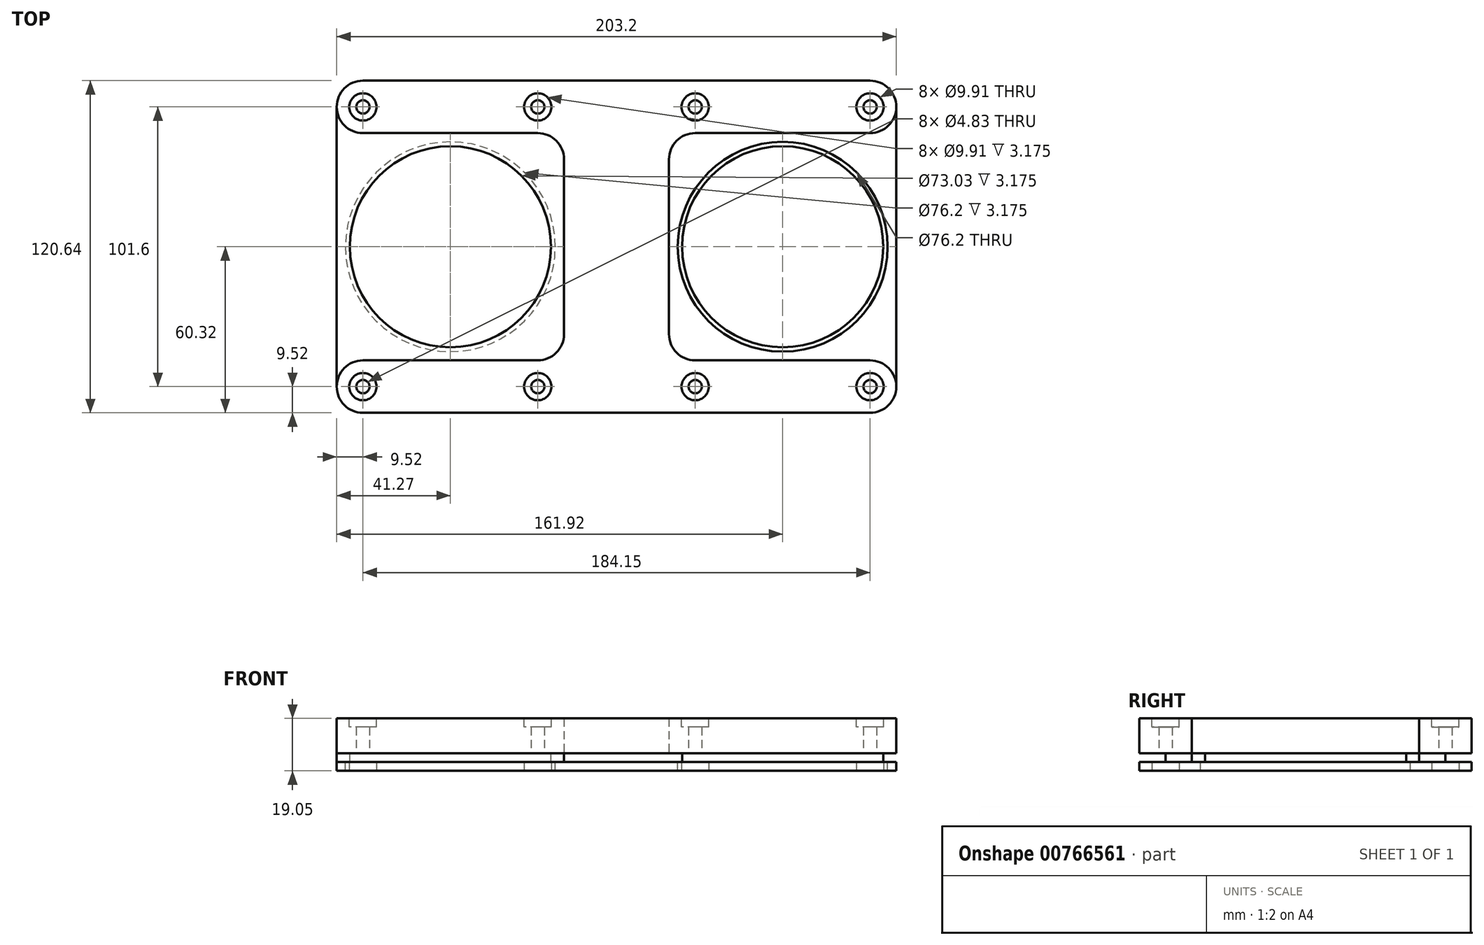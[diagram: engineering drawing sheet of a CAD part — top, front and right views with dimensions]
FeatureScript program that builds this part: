
annotation { "Feature Type Name" : "Feature", "Feature Type Description" : "" }
export const myFeature = defineFeature(function(context is Context, id is Id, definition is map)
    precondition{}
    {
        {
            var Q0;
            Q0=qCreatedBy(makeId("Top.planeOp"),FACE);
            var sketch = newSketch(context, id + "F0", { "sketchPlane" : qUnion([Q0])});
            skLineSegment(sketch, "E0.bottom", {"start": v(-31.75, -41.28) * mm, "end": v(31.75, -41.28) * mm});
            skLineSegment(sketch, "E0.top", {"start": v(-31.75, 41.28) * mm, "end": v(31.75, 41.28) * mm});
            skLineSegment(sketch, "E0.right", {"start": v(41.28, -31.75) * mm, "end": v(41.27, 31.75) * mm});
            skCircle(sketch, "E1", {"center": v(-31.75, -31.75) * mm, "radius": 4.76 * mm});
            skCircle(sketch, "E2", {"center": v(31.75, -31.75) * mm, "radius": 4.76 * mm});
            skCircle(sketch, "E3", {"center": v(31.75, 31.75) * mm, "radius": 4.76 * mm});
            skCircle(sketch, "E4", {"center": v(-31.75, 31.75) * mm, "radius": 4.76 * mm});
            skPoint(sketch, "E5.visualSharp", {"position": v(-41.28, 41.28) * mm});
            skPoint(sketch, "E6.visualSharp", {"position": v(41.28, 41.28) * mm});
            skArc(sketch, "E6.filletArc", {"start": v(41.28, 31.75) * mm, "mid": v(38.49, 38.49) * mm, "end": v(31.75, 41.28) * mm});
            skPoint(sketch, "E7.visualSharp", {"position": v(41.28, -41.28) * mm});
            skArc(sketch, "E7.filletArc", {"start": v(31.75, -41.27) * mm, "mid": v(38.49, -38.49) * mm, "end": v(41.27, -31.75) * mm});
            skPoint(sketch, "E8.visualSharp", {"position": v(-41.27, -41.28) * mm});
            skLineSegment(sketch, "E9.0", {"start": v(-31.75, -60.33) * mm, "end": v(31.75, -60.33) * mm});
            skLineSegment(sketch, "E9.1", {"start": v(-31.75, 60.33) * mm, "end": v(31.75, 60.33) * mm});
            skArc(sketch, "E10", {"start": v(-31.75, 60.33) * mm, "mid": v(-41.28, 50.8) * mm, "end": v(-31.75, 41.28) * mm});
            skCircle(sketch, "E11", {"center": v(-31.75, 50.8) * mm, "radius": 2.41 * mm});
            skCircle(sketch, "E12", {"center": v(31.75, 50.8) * mm, "radius": 2.41 * mm});
            skArc(sketch, "E13", {"start": v(-31.75, -41.28) * mm, "mid": v(-41.27, -50.8) * mm, "end": v(-31.75, -60.33) * mm});
            skCircle(sketch, "E14", {"center": v(-31.75, -50.8) * mm, "radius": 2.41 * mm});
            skCircle(sketch, "E15", {"center": v(31.75, -50.8) * mm, "radius": 2.41 * mm});
            skLineSegment(sketch, "E16.MirrorCS", {"start": v(152.4, -60.32) * mm, "end": v(88.9, -60.32) * mm});
            skLineSegment(sketch, "E17.MirrorCS", {"start": v(152.4, -41.27) * mm, "end": v(88.9, -41.27) * mm});
            skPoint(sketch, "E18.MirrorP", {"position": v(79.38, -41.27) * mm});
            skArc(sketch, "E19.MirrorCS", {"start": v(88.9, -41.27) * mm, "mid": v(82.16, -38.49) * mm, "end": v(79.38, -31.75) * mm});
            skArc(sketch, "E20.MirrorCS", {"start": v(79.37, 31.75) * mm, "mid": v(82.16, 38.49) * mm, "end": v(88.9, 41.28) * mm});
            skLineSegment(sketch, "E21.MirrorCS", {"start": v(152.4, 41.28) * mm, "end": v(88.9, 41.28) * mm});
            skCircle(sketch, "E22.MirrorC", {"center": v(152.4, 50.8) * mm, "radius": 2.41 * mm});
            skCircle(sketch, "E23.MirrorC", {"center": v(88.9, -50.8) * mm, "radius": 2.41 * mm});
            skCircle(sketch, "E24.MirrorC", {"center": v(88.9, 50.8) * mm, "radius": 2.41 * mm});
            skArc(sketch, "E25.MirrorCS", {"start": v(152.4, -41.27) * mm, "mid": v(161.93, -50.8) * mm, "end": v(152.4, -60.32) * mm});
            skCircle(sketch, "E26.MirrorC", {"center": v(152.4, -50.8) * mm, "radius": 2.41 * mm});
            skCircle(sketch, "E27.MirrorC", {"center": v(152.4, 31.75) * mm, "radius": 4.76 * mm});
            skCircle(sketch, "E28.MirrorC", {"center": v(152.4, -31.75) * mm, "radius": 4.76 * mm});
            skLineSegment(sketch, "E29.MirrorCS", {"start": v(152.4, 60.33) * mm, "end": v(88.9, 60.33) * mm});
            skPoint(sketch, "E30.MirrorP", {"position": v(161.93, 41.28) * mm});
            skArc(sketch, "E31.MirrorCS", {"start": v(152.4, 60.33) * mm, "mid": v(161.92, 50.8) * mm, "end": v(152.4, 41.28) * mm});
            skPoint(sketch, "E32.MirrorP", {"position": v(79.37, 41.28) * mm});
            skPoint(sketch, "E33.MirrorP", {"position": v(161.93, -41.27) * mm});
            skCircle(sketch, "E34.MirrorC", {"center": v(88.9, -31.75) * mm, "radius": 4.76 * mm});
            skCircle(sketch, "E35.MirrorC", {"center": v(88.9, 31.75) * mm, "radius": 4.76 * mm});
            skLineSegment(sketch, "E36.MirrorCS", {"start": v(79.38, -31.75) * mm, "end": v(79.38, 31.75) * mm});
            skLineSegment(sketch, "E37", {"start": v(31.75, 60.33) * mm, "end": v(88.9, 60.33) * mm});
            skLineSegment(sketch, "E38", {"start": v(31.75, -60.33) * mm, "end": v(88.9, -60.33) * mm});
            skPoint(sketch, "E39.MirrorCS.end.orphan", {"position": v(60.33, -31.75) * mm});
            skSolve(sketch);
        }
        {
            var Q0;
            Q0=makeQuery(id+"F0.imprint","IMPRINT",FACE,{"disambiguationData":[TD([[makeQuery(id+"F0.imprint","IMPRINT",EDGE,{"derivedFrom":sQuery(id+"F0.wireOp",EDGE,"E0.bottom")}),-1.0]])]});
            extrude(context, id + "F1", {"entities" : qUnion([Q0]), "depth" : 12.7 * mm, "offsetDistance" : 25.4 * mm});
        }
        {
            var Q0;
            Q0=makeQuery(id+"F1.opExtrude","CAP_FACE",FACE,{"disambiguationData":[OSD([sQuery(id+"F0.wireOp",EDGE,"E0.bottom"),sQuery(id+"F0.wireOp",EDGE,"E0.top"),sQuery(id+"F0.wireOp",EDGE,"E0.right"),sQuery(id+"F0.wireOp",EDGE,"E6.filletArc"),sQuery(id+"F0.wireOp",EDGE,"E7.filletArc"),sQuery(id+"F0.wireOp",EDGE,"E9.0"),sQuery(id+"F0.wireOp",EDGE,"E9.1"),sQuery(id+"F0.wireOp",EDGE,"E10"),sQuery(id+"F0.wireOp",EDGE,"E11"),sQuery(id+"F0.wireOp",EDGE,"E12"),sQuery(id+"F0.wireOp",EDGE,"E13"),sQuery(id+"F0.wireOp",EDGE,"E14"),sQuery(id+"F0.wireOp",EDGE,"E15"),sQuery(id+"F0.wireOp",EDGE,"E22.MirrorC"),sQuery(id+"F0.wireOp",EDGE,"E23.MirrorC"),sQuery(id+"F0.wireOp",EDGE,"E24.MirrorC"),sQuery(id+"F0.wireOp",EDGE,"E16.MirrorCS"),sQuery(id+"F0.wireOp",EDGE,"E25.MirrorCS"),sQuery(id+"F0.wireOp",EDGE,"E26.MirrorC"),sQuery(id+"F0.wireOp",EDGE,"E19.MirrorCS"),sQuery(id+"F0.wireOp",EDGE,"E20.MirrorCS"),sQuery(id+"F0.wireOp",EDGE,"E29.MirrorCS"),sQuery(id+"F0.wireOp",EDGE,"E17.MirrorCS"),sQuery(id+"F0.wireOp",EDGE,"E31.MirrorCS"),sQuery(id+"F0.wireOp",EDGE,"E21.MirrorCS"),sQuery(id+"F0.wireOp",EDGE,"E36.MirrorCS"),sQuery(id+"F0.wireOp",EDGE,"E37"),sQuery(id+"F0.wireOp",EDGE,"E38")])],"isStart":true});
            var sketch = newSketch(context, id + "F2", { "sketchPlane" : qUnion([Q0])});
            skArc(sketch, "E40.0.5", {"start": v(161.93, 50.8) * mm, "mid": v(159.14, 57.54) * mm, "end": v(152.4, 60.32) * mm});
            skLineSegment(sketch, "E40.0.6", {"start": v(152.4, 60.33) * mm, "end": v(-31.75, 60.33) * mm});
            skArc(sketch, "E40.0.7", {"start": v(-31.75, 60.33) * mm, "mid": v(-38.49, 57.54) * mm, "end": v(-41.27, 50.8) * mm});
            skArc(sketch, "E40.0.13", {"start": v(-41.28, -50.8) * mm, "mid": v(-38.49, -57.54) * mm, "end": v(-31.75, -60.33) * mm});
            skLineSegment(sketch, "E40.0.14", {"start": v(-31.75, -60.32) * mm, "end": v(152.4, -60.33) * mm});
            skArc(sketch, "E40.0.15", {"start": v(152.4, -60.33) * mm, "mid": v(159.14, -57.54) * mm, "end": v(161.92, -50.8) * mm});
            skLineSegment(sketch, "E41", {"start": v(60.33, 60.33) * mm, "end": v(60.33, 73.87) * mm});
            skCircle(sketch, "E42", {"center": v(-31.75, 50.8) * mm, "radius": 2.41 * mm});
            skCircle(sketch, "E43", {"center": v(-31.75, -50.8) * mm, "radius": 2.41 * mm});
            skCircle(sketch, "E44", {"center": v(31.75, -50.8) * mm, "radius": 2.41 * mm});
            skCircle(sketch, "E45", {"center": v(31.75, 50.8) * mm, "radius": 2.41 * mm});
            skCircle(sketch, "E46.MirrorC", {"center": v(152.4, 50.8) * mm, "radius": 2.41 * mm});
            skCircle(sketch, "E47.MirrorC", {"center": v(88.9, 50.8) * mm, "radius": 2.41 * mm});
            skCircle(sketch, "E48.MirrorC", {"center": v(152.4, -50.8) * mm, "radius": 2.41 * mm});
            skCircle(sketch, "E49.MirrorC", {"center": v(88.9, -50.8) * mm, "radius": 2.41 * mm});
            skCircle(sketch, "E50", {"center": v(0, 0) * mm, "radius": 36.51 * mm});
            skCircle(sketch, "E51.MirrorC", {"center": v(120.65, 0) * mm, "radius": 36.51 * mm});
            skLineSegment(sketch, "E52", {"start": v(-41.28, 50.8) * mm, "end": v(-41.28, -50.8) * mm});
            skLineSegment(sketch, "E53", {"start": v(161.93, 50.8) * mm, "end": v(161.92, -50.8) * mm});
            skPoint(sketch, "E54.orphan", {"position": v(-31.75, 41.28) * mm});
            skPoint(sketch, "E55.orphan", {"position": v(-31.75, -41.28) * mm});
            skPoint(sketch, "E56.orphan", {"position": v(152.4, -41.28) * mm});
            skPoint(sketch, "E57.orphan", {"position": v(152.4, 41.27) * mm});
            skSolve(sketch);
        }
        {
            var Q0;
            {var subQ6=sQuery(id+"F2.wireOp",EDGE,"E40.0.5");Q0=makeQuery(id+"F2.imprint","IMPRINT",FACE,{"disambiguationData":[TD([[makeQuery(id+"F2.imprint","IMPRINT",EDGE,{"derivedFrom":subQ6}),1.0]])]});}
            var Q1;
            Q1=makeQuery(id+"F2.imprint","IMPRINT",FACE,{"disambiguationData":[TD([[makeQuery(id+"F2.imprint","IMPRINT",EDGE,{"derivedFrom":sQuery(id+"F2.wireOp",EDGE,"E51.MirrorC")}),1.0]])]});
            var Q2;
            Q2=makeQuery(id+"F2.imprint","IMPRINT",FACE,{"disambiguationData":[TD([[makeQuery(id+"F2.imprint","IMPRINT",EDGE,{"derivedFrom":sQuery(id+"F2.wireOp",EDGE,"E50")}),-1.0]])]});
            extrude(context, id + "F3", {"entities" : qUnion([Q0, Q1, Q2]), "operationType" : NewBodyOperationType.ADD, "depth" : 3.17 * mm, "offsetDistance" : 25.4 * mm});
        }
        {
            var Q0;
            Q0=makeQuery(id+"F3.opExtrude","CAP_FACE",FACE,{"disambiguationData":[OSD([sQuery(id+"F2.wireOp",EDGE,"E40.0.5"),sQuery(id+"F2.wireOp",EDGE,"E40.0.6"),sQuery(id+"F2.wireOp",EDGE,"E40.0.7"),sQuery(id+"F2.wireOp",EDGE,"E40.0.13"),sQuery(id+"F2.wireOp",EDGE,"E40.0.14"),sQuery(id+"F2.wireOp",EDGE,"E40.0.15"),sQuery(id+"F2.wireOp",EDGE,"E42"),sQuery(id+"F2.wireOp",EDGE,"E43"),sQuery(id+"F2.wireOp",EDGE,"E44"),sQuery(id+"F2.wireOp",EDGE,"E45"),sQuery(id+"F2.wireOp",EDGE,"E47.MirrorC"),sQuery(id+"F2.wireOp",EDGE,"E46.MirrorC"),sQuery(id+"F2.wireOp",EDGE,"E48.MirrorC"),sQuery(id+"F2.wireOp",EDGE,"E49.MirrorC"),sQuery(id+"F2.wireOp",EDGE,"E50"),sQuery(id+"F2.wireOp",EDGE,"E51.MirrorC"),sQuery(id+"F2.wireOp",EDGE,"E52"),sQuery(id+"F2.wireOp",EDGE,"E53")])],"isStart":false});
            var sketch = newSketch(context, id + "F4", { "sketchPlane" : qUnion([Q0])});
            skArc(sketch, "E58.0.0", {"start": v(152.4, -60.33) * mm, "mid": v(159.14, -57.54) * mm, "end": v(161.92, -50.8) * mm});
            skLineSegment(sketch, "E58.0.1", {"start": v(161.92, -50.8) * mm, "end": v(161.93, 50.8) * mm});
            skArc(sketch, "E58.0.2", {"start": v(161.93, 50.8) * mm, "mid": v(159.14, 57.54) * mm, "end": v(152.4, 60.32) * mm});
            skLineSegment(sketch, "E58.0.3", {"start": v(152.4, 60.33) * mm, "end": v(-31.75, 60.33) * mm});
            skArc(sketch, "E58.0.4", {"start": v(-31.75, 60.33) * mm, "mid": v(-38.49, 57.54) * mm, "end": v(-41.27, 50.8) * mm});
            skLineSegment(sketch, "E58.0.5", {"start": v(-41.28, 50.8) * mm, "end": v(-41.28, -50.8) * mm});
            skArc(sketch, "E58.0.6", {"start": v(-41.28, -50.8) * mm, "mid": v(-38.49, -57.54) * mm, "end": v(-31.75, -60.33) * mm});
            skLineSegment(sketch, "E58.0.7", {"start": v(-31.75, -60.32) * mm, "end": v(152.4, -60.33) * mm});
            skCircle(sketch, "E59", {"center": v(0, 0) * mm, "radius": 38.1 * mm});
            skCircle(sketch, "E60", {"center": v(120.65, 0) * mm, "radius": 38.1 * mm});
            skLineSegment(sketch, "E61.0.0", {"start": v(88.9, -41.28) * mm, "end": v(152.4, -41.28) * mm});
            skArc(sketch, "E61.0.1", {"start": v(152.4, -41.28) * mm, "mid": v(161.92, -50.8) * mm, "end": v(152.4, -60.33) * mm});
            skLineSegment(sketch, "E61.0.2", {"start": v(152.4, -60.33) * mm, "end": v(-31.75, -60.32) * mm});
            skArc(sketch, "E61.0.3", {"start": v(-31.75, -60.33) * mm, "mid": v(-41.28, -50.8) * mm, "end": v(-31.75, -41.28) * mm});
            skLineSegment(sketch, "E61.0.4", {"start": v(-31.75, -41.28) * mm, "end": v(31.75, -41.28) * mm});
            skArc(sketch, "E61.0.5", {"start": v(31.75, -41.28) * mm, "mid": v(38.49, -38.49) * mm, "end": v(41.28, -31.75) * mm});
            skLineSegment(sketch, "E61.0.6", {"start": v(41.27, -31.75) * mm, "end": v(41.28, 31.75) * mm});
            skArc(sketch, "E61.0.7", {"start": v(41.27, 31.75) * mm, "mid": v(38.49, 38.49) * mm, "end": v(31.75, 41.27) * mm});
            skLineSegment(sketch, "E61.0.8", {"start": v(31.75, 41.28) * mm, "end": v(-31.75, 41.28) * mm});
            skArc(sketch, "E61.0.9", {"start": v(-31.75, 41.28) * mm, "mid": v(-41.27, 50.8) * mm, "end": v(-31.75, 60.33) * mm});
            skLineSegment(sketch, "E61.0.10", {"start": v(-31.75, 60.33) * mm, "end": v(152.4, 60.33) * mm});
            skArc(sketch, "E61.0.11", {"start": v(152.4, 60.32) * mm, "mid": v(161.93, 50.8) * mm, "end": v(152.4, 41.27) * mm});
            skLineSegment(sketch, "E61.0.12", {"start": v(152.4, 41.27) * mm, "end": v(88.9, 41.27) * mm});
            skArc(sketch, "E61.0.13", {"start": v(88.9, 41.27) * mm, "mid": v(82.16, 38.49) * mm, "end": v(79.38, 31.75) * mm});
            skLineSegment(sketch, "E61.0.14", {"start": v(79.38, 31.75) * mm, "end": v(79.38, -31.75) * mm});
            skArc(sketch, "E61.0.15", {"start": v(79.37, -31.75) * mm, "mid": v(82.16, -38.49) * mm, "end": v(88.9, -41.28) * mm});
            skCircle(sketch, "E62", {"center": v(152.4, -50.8) * mm, "radius": 2.8 * mm});
            skCircle(sketch, "E63.0.0", {"center": v(31.75, -50.8) * mm, "radius": 2.8 * mm});
            skCircle(sketch, "E64.0.0", {"center": v(-31.75, -50.8) * mm, "radius": 2.8 * mm});
            skCircle(sketch, "E65.0.0", {"center": v(88.9, 50.8) * mm, "radius": 2.8 * mm});
            skCircle(sketch, "E66.0", {"center": v(152.4, 50.8) * mm, "radius": 2.8 * mm});
            skCircle(sketch, "E67.0", {"center": v(-31.75, 50.8) * mm, "radius": 2.8 * mm});
            skCircle(sketch, "E68.0", {"center": v(31.75, 50.8) * mm, "radius": 2.8 * mm});
            skCircle(sketch, "E69", {"center": v(88.9, -50.8) * mm, "radius": 2.8 * mm});
            skSolve(sketch);
        }
        {
            var Q0;
            {var subQ12=sQuery(id+"F4.wireOp",EDGE,"E61.0.0");Q0=makeQuery(id+"F4.imprint","IMPRINT",FACE,{"disambiguationData":[TD([[makeQuery(id+"F4.imprint","IMPRINT",EDGE,{"derivedFrom":subQ12}),-1.0]])]});}
            var Q1;
            Q1=makeQuery(id+"F4.imprint","IMPRINT",FACE,{"disambiguationData":[TD([[makeQuery(id+"F4.imprint","IMPRINT",EDGE,{"derivedFrom":sQuery(id+"F4.wireOp",EDGE,"E59")}),-1.0]])]});
            var Q2;
            Q2=makeQuery(id+"F4.imprint","IMPRINT",FACE,{"disambiguationData":[TD([[makeQuery(id+"F4.imprint","IMPRINT",EDGE,{"derivedFrom":sQuery(id+"F4.wireOp",EDGE,"E60")}),-1.0]])]});
            extrude(context, id + "F5", {"entities" : qUnion([Q0, Q1, Q2]), "operationType" : NewBodyOperationType.ADD, "depth" : 3.17 * mm, "offsetDistance" : 25.4 * mm});
        }
        {
            var Q0;
            Q0=makeQuery(id+"F1.opExtrude","CAP_FACE",FACE,{"disambiguationData":[OSD([sQuery(id+"F0.wireOp",EDGE,"E0.bottom"),sQuery(id+"F0.wireOp",EDGE,"E0.top"),sQuery(id+"F0.wireOp",EDGE,"E0.right"),sQuery(id+"F0.wireOp",EDGE,"E6.filletArc"),sQuery(id+"F0.wireOp",EDGE,"E7.filletArc"),sQuery(id+"F0.wireOp",EDGE,"E9.0"),sQuery(id+"F0.wireOp",EDGE,"E9.1"),sQuery(id+"F0.wireOp",EDGE,"E10"),sQuery(id+"F0.wireOp",EDGE,"E11"),sQuery(id+"F0.wireOp",EDGE,"E12"),sQuery(id+"F0.wireOp",EDGE,"E13"),sQuery(id+"F0.wireOp",EDGE,"E14"),sQuery(id+"F0.wireOp",EDGE,"E15"),sQuery(id+"F0.wireOp",EDGE,"E22.MirrorC"),sQuery(id+"F0.wireOp",EDGE,"E23.MirrorC"),sQuery(id+"F0.wireOp",EDGE,"E24.MirrorC"),sQuery(id+"F0.wireOp",EDGE,"E16.MirrorCS"),sQuery(id+"F0.wireOp",EDGE,"E25.MirrorCS"),sQuery(id+"F0.wireOp",EDGE,"E26.MirrorC"),sQuery(id+"F0.wireOp",EDGE,"E19.MirrorCS"),sQuery(id+"F0.wireOp",EDGE,"E20.MirrorCS"),sQuery(id+"F0.wireOp",EDGE,"E29.MirrorCS"),sQuery(id+"F0.wireOp",EDGE,"E17.MirrorCS"),sQuery(id+"F0.wireOp",EDGE,"E31.MirrorCS"),sQuery(id+"F0.wireOp",EDGE,"E21.MirrorCS"),sQuery(id+"F0.wireOp",EDGE,"E36.MirrorCS"),sQuery(id+"F0.wireOp",EDGE,"E37"),sQuery(id+"F0.wireOp",EDGE,"E38")])],"isStart":false});
            var sketch = newSketch(context, id + "F6", { "sketchPlane" : qUnion([Q0])});
            skPoint(sketch, "E70", {"position": v(152.4, -50.8) * mm});
            skPoint(sketch, "E71", {"position": v(88.9, -50.8) * mm});
            skPoint(sketch, "E72", {"position": v(31.75, -50.8) * mm});
            skPoint(sketch, "E73", {"position": v(-31.75, -50.8) * mm});
            skPoint(sketch, "E74", {"position": v(-31.75, 50.8) * mm});
            skPoint(sketch, "E75", {"position": v(31.75, 50.8) * mm});
            skPoint(sketch, "E76", {"position": v(88.9, 50.8) * mm});
            skPoint(sketch, "E77", {"position": v(152.4, 50.8) * mm});
            skCircle(sketch, "E78", {"center": v(-31.75, 50.8) * mm, "radius": 4.95 * mm});
            skCircle(sketch, "E79", {"center": v(31.75, 50.8) * mm, "radius": 4.95 * mm});
            skCircle(sketch, "E80", {"center": v(88.9, 50.8) * mm, "radius": 4.95 * mm});
            skCircle(sketch, "E81", {"center": v(152.4, 50.8) * mm, "radius": 4.95 * mm});
            skCircle(sketch, "E82", {"center": v(-31.75, -50.8) * mm, "radius": 4.95 * mm});
            skCircle(sketch, "E83", {"center": v(31.75, -50.8) * mm, "radius": 4.95 * mm});
            skCircle(sketch, "E84", {"center": v(88.9, -50.8) * mm, "radius": 4.95 * mm});
            skCircle(sketch, "E85", {"center": v(152.4, -50.8) * mm, "radius": 4.95 * mm});
            skSolve(sketch);
        }
        {
            var Q0;
            Q0=makeQuery(id+"F6.imprint","IMPRINT",FACE,{"disambiguationData":[TD([[makeQuery(id+"F6.imprint","IMPRINT",EDGE,{"derivedFrom":sQuery(id+"F6.wireOp",EDGE,"E78")}),1.0]])]});
            var Q1;
            Q1=makeQuery(id+"F6.imprint","IMPRINT",FACE,{"disambiguationData":[TD([[makeQuery(id+"F6.imprint","IMPRINT",EDGE,{"derivedFrom":sQuery(id+"F6.wireOp",EDGE,"E79")}),1.0]])]});
            var Q2;
            Q2=makeQuery(id+"F6.imprint","IMPRINT",FACE,{"disambiguationData":[TD([[makeQuery(id+"F6.imprint","IMPRINT",EDGE,{"derivedFrom":sQuery(id+"F6.wireOp",EDGE,"E80")}),1.0]])]});
            var Q3;
            Q3=makeQuery(id+"F6.imprint","IMPRINT",FACE,{"disambiguationData":[TD([[makeQuery(id+"F6.imprint","IMPRINT",EDGE,{"derivedFrom":sQuery(id+"F6.wireOp",EDGE,"E81")}),1.0]])]});
            var Q4;
            Q4=makeQuery(id+"F6.imprint","IMPRINT",FACE,{"disambiguationData":[TD([[makeQuery(id+"F6.imprint","IMPRINT",EDGE,{"derivedFrom":sQuery(id+"F6.wireOp",EDGE,"E82")}),1.0]])]});
            var Q5;
            Q5=makeQuery(id+"F6.imprint","IMPRINT",FACE,{"disambiguationData":[TD([[makeQuery(id+"F6.imprint","IMPRINT",EDGE,{"derivedFrom":sQuery(id+"F6.wireOp",EDGE,"E83")}),1.0]])]});
            var Q6;
            Q6=makeQuery(id+"F6.imprint","IMPRINT",FACE,{"disambiguationData":[TD([[makeQuery(id+"F6.imprint","IMPRINT",EDGE,{"derivedFrom":sQuery(id+"F6.wireOp",EDGE,"E84")}),1.0]])]});
            var Q7;
            Q7=makeQuery(id+"F6.imprint","IMPRINT",FACE,{"disambiguationData":[TD([[makeQuery(id+"F6.imprint","IMPRINT",EDGE,{"derivedFrom":sQuery(id+"F6.wireOp",EDGE,"E85")}),1.0]])]});
            extrude(context, id + "F7", {"entities" : qUnion([Q0, Q1, Q2, Q3, Q4, Q5, Q6, Q7]), "operationType" : NewBodyOperationType.REMOVE, "oppositeDirection" : true, "depth" : 3.17 * mm, "offsetDistance" : 25.4 * mm});
        }
        {
            var Q0;
            Q0=makeQuery(id+"F5.opExtrude","CAP_FACE",FACE,{"disambiguationData":[OSD([sQuery(id+"F4.wireOp",EDGE,"E59"),sQuery(id+"F4.wireOp",EDGE,"E60"),sQuery(id+"F4.wireOp",EDGE,"E58.0.1"),sQuery(id+"F4.wireOp",EDGE,"E58.0.5"),sQuery(id+"F4.wireOp",EDGE,"E61.0.1"),sQuery(id+"F4.wireOp",EDGE,"E61.0.2"),sQuery(id+"F4.wireOp",EDGE,"E61.0.3"),sQuery(id+"F4.wireOp",EDGE,"E61.0.9"),sQuery(id+"F4.wireOp",EDGE,"E61.0.10"),sQuery(id+"F4.wireOp",EDGE,"E61.0.11"),sQuery(id+"F4.wireOp",EDGE,"E62"),sQuery(id+"F4.wireOp",EDGE,"066266e3-139a-4e70-843c-53a09532814f.0"),sQuery(id+"F4.wireOp",EDGE,"E63.0.0"),sQuery(id+"F4.wireOp",EDGE,"E64.0.0"),sQuery(id+"F4.wireOp",EDGE,"E65.0.0"),sQuery(id+"F4.wireOp",EDGE,"E66.0"),sQuery(id+"F4.wireOp",EDGE,"E67.0"),sQuery(id+"F4.wireOp",EDGE,"E68.0")])],"isStart":false});
            var sketch = newSketch(context, id + "F8", { "sketchPlane" : qUnion([Q0])});
            skCircle(sketch, "E86", {"center": v(-31.75, 50.8) * mm, "radius": 4.95 * mm});
            skCircle(sketch, "E87", {"center": v(31.75, 50.8) * mm, "radius": 4.95 * mm});
            skCircle(sketch, "E88", {"center": v(88.9, 50.8) * mm, "radius": 4.95 * mm});
            skCircle(sketch, "E89", {"center": v(152.4, 50.8) * mm, "radius": 4.95 * mm});
            skCircle(sketch, "E90", {"center": v(-31.75, -50.8) * mm, "radius": 4.95 * mm});
            skCircle(sketch, "E91", {"center": v(31.75, -50.8) * mm, "radius": 4.95 * mm});
            skCircle(sketch, "E92", {"center": v(88.9, -50.8) * mm, "radius": 4.95 * mm});
            skCircle(sketch, "E93", {"center": v(152.4, -50.8) * mm, "radius": 4.95 * mm});
            skSolve(sketch);
        }
        {
            var Q0;
            Q0=makeQuery(id+"F8.imprint","IMPRINT",FACE,{"disambiguationData":[TD([[makeQuery(id+"F8.imprint","IMPRINT",EDGE,{"derivedFrom":sQuery(id+"F8.wireOp",EDGE,"E86")}),1.0]])]});
            var Q1;
            Q1=makeQuery(id+"F8.imprint","IMPRINT",FACE,{"disambiguationData":[TD([[makeQuery(id+"F8.imprint","IMPRINT",EDGE,{"derivedFrom":sQuery(id+"F8.wireOp",EDGE,"E87")}),1.0]])]});
            var Q2;
            Q2=makeQuery(id+"F8.imprint","IMPRINT",FACE,{"disambiguationData":[TD([[makeQuery(id+"F8.imprint","IMPRINT",EDGE,{"derivedFrom":sQuery(id+"F8.wireOp",EDGE,"E88")}),1.0]])]});
            var Q3;
            Q3=makeQuery(id+"F8.imprint","IMPRINT",FACE,{"disambiguationData":[TD([[makeQuery(id+"F8.imprint","IMPRINT",EDGE,{"derivedFrom":sQuery(id+"F8.wireOp",EDGE,"E89")}),1.0]])]});
            var Q4;
            Q4=makeQuery(id+"F8.imprint","IMPRINT",FACE,{"disambiguationData":[TD([[makeQuery(id+"F8.imprint","IMPRINT",EDGE,{"derivedFrom":sQuery(id+"F8.wireOp",EDGE,"E90")}),1.0]])]});
            var Q5;
            Q5=makeQuery(id+"F8.imprint","IMPRINT",FACE,{"disambiguationData":[TD([[makeQuery(id+"F8.imprint","IMPRINT",EDGE,{"derivedFrom":sQuery(id+"F8.wireOp",EDGE,"E91")}),1.0]])]});
            var Q6;
            Q6=makeQuery(id+"F8.imprint","IMPRINT",FACE,{"disambiguationData":[TD([[makeQuery(id+"F8.imprint","IMPRINT",EDGE,{"derivedFrom":sQuery(id+"F8.wireOp",EDGE,"E92")}),1.0]])]});
            var Q7;
            Q7=makeQuery(id+"F8.imprint","IMPRINT",FACE,{"disambiguationData":[TD([[makeQuery(id+"F8.imprint","IMPRINT",EDGE,{"derivedFrom":sQuery(id+"F8.wireOp",EDGE,"E93")}),1.0]])]});
            extrude(context, id + "F9", {"entities" : qUnion([Q0, Q1, Q2, Q3, Q4, Q5, Q6, Q7]), "operationType" : NewBodyOperationType.REMOVE, "oppositeDirection" : true, "depth" : 3.17 * mm, "offsetDistance" : 25.4 * mm});
        }
    });
